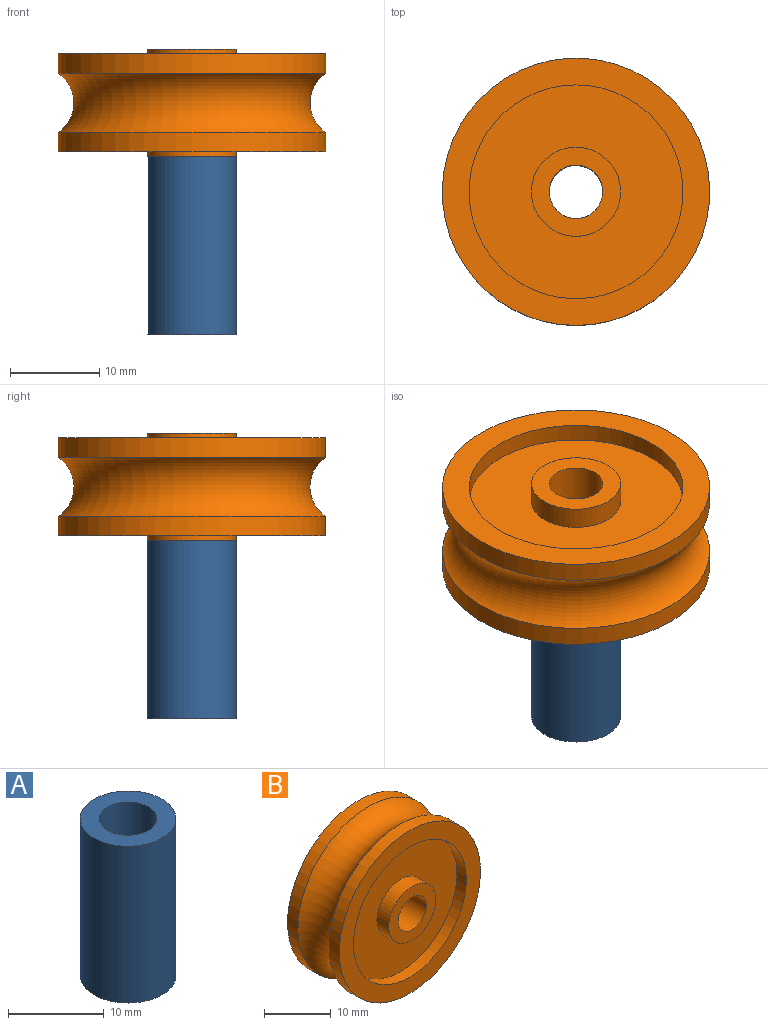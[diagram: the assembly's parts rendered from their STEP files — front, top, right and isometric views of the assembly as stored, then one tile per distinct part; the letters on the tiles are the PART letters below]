
ASSEMBLY  parts=2 mates=1
PART A: 4 faces, bbox 10x10x20 mm
  f0: cylinder r=3mm len=20mm, axis (0,0,-1), area 377mm2, adj f2,f3
  f1: cylinder r=5mm len=20mm, axis (0,0,-1), area 628.3mm2, adj f2,f3
  f2: plane 10x10mm, normal (0,0,1), area 50.3mm2, adj f0,f1
  f3: plane 10x10mm, normal (0,0,-1), area 50.3mm2, adj f0,f1
PART B: 14 faces, bbox 37.3x12x37.3 mm
  f0: torus R=17.25mm, axis (0,1,0), area 677.8mm2, adj f1,f8
  f1: cylinder r=15mm len=30mm, axis (0,1,0), area 206.7mm2, adj f0,f2
  f2: plane 30x30mm, normal (0,-1,0), area 254.5mm2, adj f1,f3
  f3: cylinder r=12mm len=24mm, axis (0,-1,0), area 150.8mm2, adj f2,f4
  f4: plane 24x24mm, normal (0,-1,0), area 373.8mm2, adj f3,f7
  f5: cylinder r=3mm len=12mm, axis (0,1,0), area 226.2mm2, adj f6,f12
  f6: plane 10x10mm, normal (0,-1,0), area 50.3mm2, adj f5,f7
  f7: cylinder r=5mm len=10mm, axis (0,1,0), area 78.5mm2, adj f4,f6
  f8: cylinder r=15mm len=30mm, axis (0,-1,0), area 206.7mm2, adj f0,f9
  f9: plane 30x30mm, normal (0,1,0), area 254.5mm2, adj f8,f10
  f10: cylinder r=12mm len=24mm, axis (0,1,0), area 150.8mm2, adj f9,f11
  f11: plane 24x24mm, normal (0,1,0), area 373.8mm2, adj f10,f13
  f12: plane 10x10mm, normal (0,1,0), area 50.3mm2, adj f5,f13
  f13: cylinder r=5mm len=10mm, axis (0,-1,0), area 78.5mm2, adj f11,f12
PLACE A t=(28.1,48.95,-3.15)mm
PLACE B rot(axis=(1,0,0),90deg) t=(-12.69,-6.68,22.85)mm
MATE fastened B.f5 <-> A.f0  axis (0,0,-1) through (-12.69,-6.68,16.85)mm
